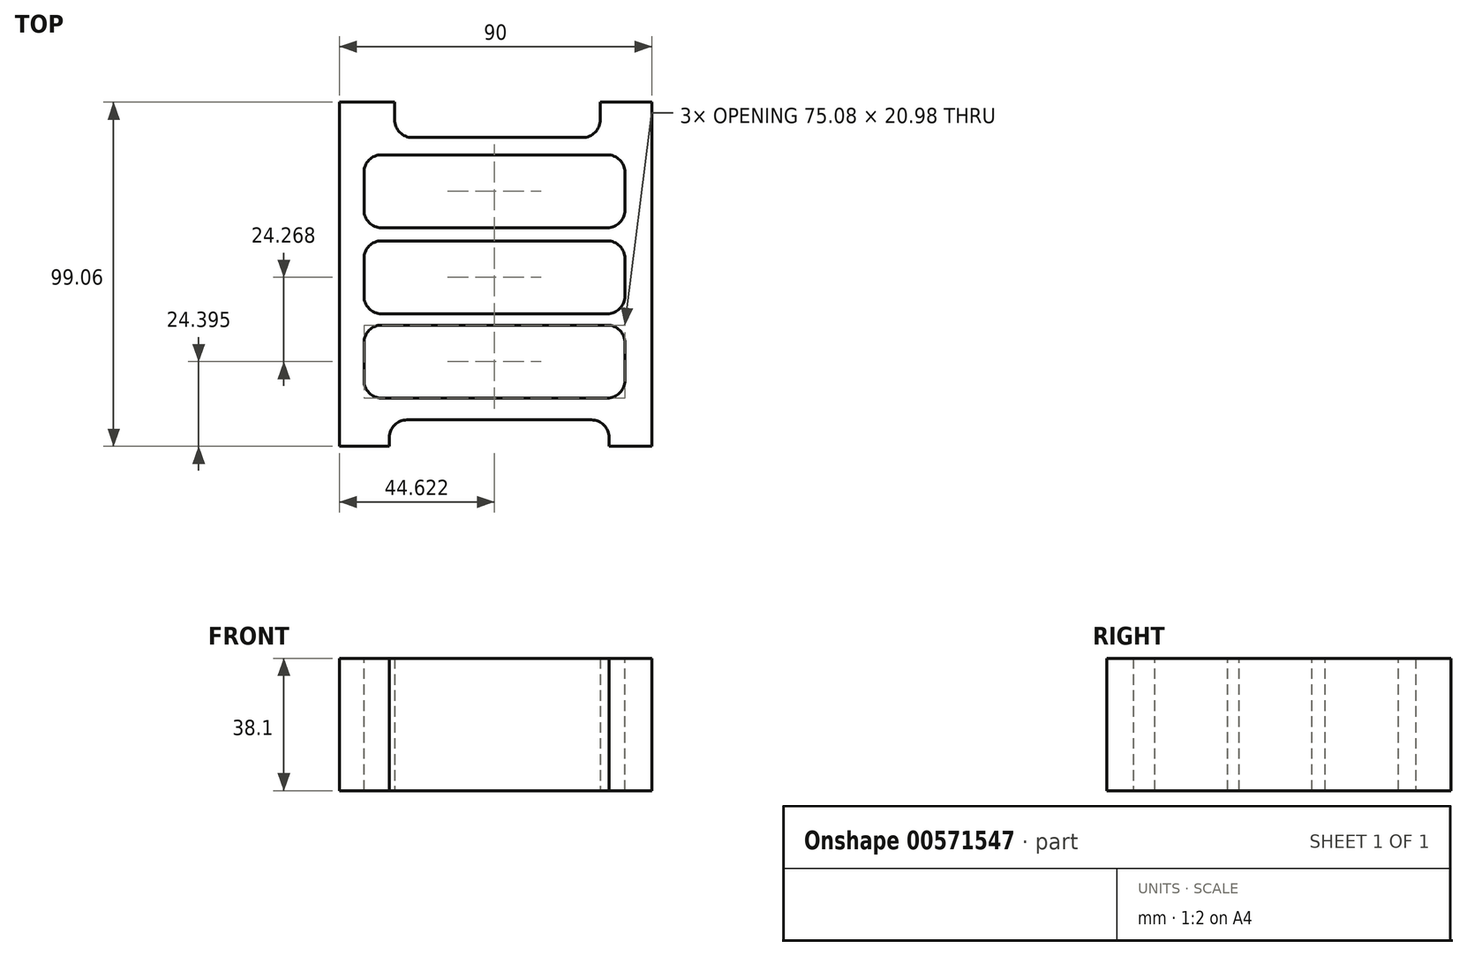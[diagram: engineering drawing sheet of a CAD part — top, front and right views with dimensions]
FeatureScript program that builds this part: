
annotation { "Feature Type Name" : "Feature", "Feature Type Description" : "" }
export const myFeature = defineFeature(function(context is Context, id is Id, definition is map)
    precondition{}
    {
        {
            var Q0;
            Q0=qCreatedBy(makeId("Top.planeOp"),FACE);
            var sketch = newSketch(context, id + "F0", { "sketchPlane" : qUnion([Q0])});
            skLineSegment(sketch, "E0.bottom", {"start": v(-48.92, 48.88) * mm, "end": v(41.08, 48.88) * mm});
            skLineSegment(sketch, "E0.top", {"start": v(-48.92, -50.18) * mm, "end": v(41.08, -50.18) * mm});
            skLineSegment(sketch, "E0.left", {"start": v(-48.92, 48.88) * mm, "end": v(-48.92, -50.18) * mm});
            skLineSegment(sketch, "E0.right", {"start": v(41.08, 48.88) * mm, "end": v(41.08, -50.18) * mm});
            skSolve(sketch);
        }
        {
            var Q0;
            Q0=makeQuery(id+"F0.imprint","IMPRINT",FACE,{"disambiguationData":[TD([[makeQuery(id+"F0.imprint","IMPRINT",EDGE,{"derivedFrom":sQuery(id+"F0.wireOp",EDGE,"E0.bottom")}),-1.0]])]});
            extrude(context, id + "F1", {"entities" : qUnion([Q0]), "depth" : 38.1 * mm, "offsetDistance" : 25.4 * mm});
        }
        {
            var Q0;
            Q0=makeQuery(id+"F1.opExtrude","CAP_FACE",FACE,{"disambiguationData":[OSD([sQuery(id+"F0.wireOp",EDGE,"E0.bottom"),sQuery(id+"F0.wireOp",EDGE,"E0.top"),sQuery(id+"F0.wireOp",EDGE,"E0.left"),sQuery(id+"F0.wireOp",EDGE,"E0.right")])],"isStart":false});
            var sketch = newSketch(context, id + "F2", { "sketchPlane" : qUnion([Q0])});
            skLineSegment(sketch, "E1.bottom", {"start": v(-41.84, 33.75) * mm, "end": v(33.24, 33.75) * mm});
            skLineSegment(sketch, "E1.top", {"start": v(-41.84, 12.77) * mm, "end": v(33.24, 12.77) * mm});
            skLineSegment(sketch, "E1.left", {"start": v(-41.84, 33.75) * mm, "end": v(-41.84, 12.77) * mm});
            skLineSegment(sketch, "E1.right", {"start": v(33.24, 33.75) * mm, "end": v(33.24, 12.77) * mm});
            skLineSegment(sketch, "E2.bottom", {"start": v(-41.84, 8.97) * mm, "end": v(33.24, 8.97) * mm});
            skLineSegment(sketch, "E2.top", {"start": v(-41.84, -12) * mm, "end": v(33.24, -12) * mm});
            skLineSegment(sketch, "E2.left", {"start": v(-41.84, 8.97) * mm, "end": v(-41.84, -12) * mm});
            skLineSegment(sketch, "E2.right", {"start": v(33.24, 8.97) * mm, "end": v(33.24, -12) * mm});
            skLineSegment(sketch, "E3.bottom", {"start": v(-41.84, -15.3) * mm, "end": v(33.24, -15.3) * mm});
            skLineSegment(sketch, "E3.top", {"start": v(-41.84, -36.28) * mm, "end": v(33.24, -36.28) * mm});
            skLineSegment(sketch, "E3.left", {"start": v(-41.84, -15.3) * mm, "end": v(-41.84, -36.28) * mm});
            skLineSegment(sketch, "E3.right", {"start": v(33.24, -15.3) * mm, "end": v(33.24, -36.28) * mm});
            skSolve(sketch);
        }
        {
            var Q0;
            Q0=makeQuery(id+"F2.imprint","IMPRINT",FACE,{"disambiguationData":[TD([[makeQuery(id+"F2.imprint","IMPRINT",EDGE,{"derivedFrom":sQuery(id+"F2.wireOp",EDGE,"E1.bottom")}),-1.0]])]});
            var Q1;
            Q1=makeQuery(id+"F2.imprint","IMPRINT",FACE,{"disambiguationData":[TD([[makeQuery(id+"F2.imprint","IMPRINT",EDGE,{"derivedFrom":sQuery(id+"F2.wireOp",EDGE,"E2.bottom")}),-1.0]])]});
            var Q2;
            Q2=makeQuery(id+"F2.imprint","IMPRINT",FACE,{"disambiguationData":[TD([[makeQuery(id+"F2.imprint","IMPRINT",EDGE,{"derivedFrom":sQuery(id+"F2.wireOp",EDGE,"E3.bottom")}),-1.0]])]});
            extrude(context, id + "F3", {"entities" : qUnion([Q0, Q1, Q2]), "operationType" : NewBodyOperationType.REMOVE, "oppositeDirection" : true, "depth" : 38.1 * mm, "offsetDistance" : 25.4 * mm});
        }
        {
            var Q0;
            Q0=makeQuery(id+"F3.boolean.opBoolean","COPY",EDGE,{"derivedFrom":makeQuery(id+"F3.opExtrude","SWEPT_EDGE",EDGE,{"disambiguationData":[OSD([sQuery(id+"F2.wireOp",EDGE,"E1.bottom"),sQuery(id+"F2.wireOp",EDGE,"E1.right")])]})});
            var Q1;
            Q1=makeQuery(id+"F3.boolean.opBoolean","COPY",EDGE,{"derivedFrom":makeQuery(id+"F3.opExtrude","SWEPT_EDGE",EDGE,{"disambiguationData":[OSD([sQuery(id+"F2.wireOp",EDGE,"E2.bottom"),sQuery(id+"F2.wireOp",EDGE,"E2.right")])]})});
            var Q2;
            Q2=makeQuery(id+"F3.boolean.opBoolean","COPY",EDGE,{"derivedFrom":makeQuery(id+"F3.opExtrude","SWEPT_EDGE",EDGE,{"disambiguationData":[OSD([sQuery(id+"F2.wireOp",EDGE,"E3.bottom"),sQuery(id+"F2.wireOp",EDGE,"E3.right")])]})});
            var Q3;
            Q3=makeQuery(id+"F3.boolean.opBoolean","COPY",EDGE,{"derivedFrom":makeQuery(id+"F3.opExtrude","SWEPT_EDGE",EDGE,{"disambiguationData":[OSD([sQuery(id+"F2.wireOp",EDGE,"E1.bottom"),sQuery(id+"F2.wireOp",EDGE,"E1.left")])]})});
            var Q4;
            Q4=makeQuery(id+"F3.boolean.opBoolean","COPY",EDGE,{"derivedFrom":makeQuery(id+"F3.opExtrude","SWEPT_EDGE",EDGE,{"disambiguationData":[OSD([sQuery(id+"F2.wireOp",EDGE,"E2.bottom"),sQuery(id+"F2.wireOp",EDGE,"E2.left")])]})});
            var Q5;
            Q5=makeQuery(id+"F3.boolean.opBoolean","COPY",EDGE,{"derivedFrom":makeQuery(id+"F3.opExtrude","SWEPT_EDGE",EDGE,{"disambiguationData":[OSD([sQuery(id+"F2.wireOp",EDGE,"E3.bottom"),sQuery(id+"F2.wireOp",EDGE,"E3.left")])]})});
            var Q6;
            Q6=makeQuery(id+"F3.boolean.opBoolean","COPY",EDGE,{"derivedFrom":makeQuery(id+"F3.opExtrude","SWEPT_EDGE",EDGE,{"disambiguationData":[OSD([sQuery(id+"F2.wireOp",EDGE,"E3.top"),sQuery(id+"F2.wireOp",EDGE,"E3.left")])]})});
            var Q7;
            Q7=makeQuery(id+"F3.boolean.opBoolean","COPY",EDGE,{"derivedFrom":makeQuery(id+"F3.opExtrude","SWEPT_EDGE",EDGE,{"disambiguationData":[OSD([sQuery(id+"F2.wireOp",EDGE,"E2.top"),sQuery(id+"F2.wireOp",EDGE,"E2.left")])]})});
            var Q8;
            Q8=makeQuery(id+"F3.boolean.opBoolean","COPY",EDGE,{"derivedFrom":makeQuery(id+"F3.opExtrude","SWEPT_EDGE",EDGE,{"disambiguationData":[OSD([sQuery(id+"F2.wireOp",EDGE,"E1.top"),sQuery(id+"F2.wireOp",EDGE,"E1.left")])]})});
            var Q9;
            Q9=makeQuery(id+"F3.boolean.opBoolean","COPY",EDGE,{"derivedFrom":makeQuery(id+"F3.opExtrude","SWEPT_EDGE",EDGE,{"disambiguationData":[OSD([sQuery(id+"F2.wireOp",EDGE,"E3.top"),sQuery(id+"F2.wireOp",EDGE,"E3.right")])]})});
            var Q10;
            Q10=makeQuery(id+"F3.boolean.opBoolean","COPY",EDGE,{"derivedFrom":makeQuery(id+"F3.opExtrude","SWEPT_EDGE",EDGE,{"disambiguationData":[OSD([sQuery(id+"F2.wireOp",EDGE,"E2.top"),sQuery(id+"F2.wireOp",EDGE,"E2.right")])]})});
            var Q11;
            Q11=makeQuery(id+"F3.boolean.opBoolean","COPY",EDGE,{"derivedFrom":makeQuery(id+"F3.opExtrude","SWEPT_EDGE",EDGE,{"disambiguationData":[OSD([sQuery(id+"F2.wireOp",EDGE,"E1.top"),sQuery(id+"F2.wireOp",EDGE,"E1.right")])]})});
            fillet(context, id + "F4", {"entities" : qUnion([Q0, Q1, Q2, Q3, Q4, Q5, Q6, Q7, Q8, Q9, Q10, Q11]), "radius" : 5.08 * mm, "tangentPropagation" : true, "allowEdgeOverflow" : false});
        }
        {
            var Q0;
            Q0=makeQuery(id+"F1.opExtrude","SWEPT_FACE",FACE,{"disambiguationData":[OSD([sQuery(id+"F0.wireOp",EDGE,"E0.bottom")])]});
            var sketch = newSketch(context, id + "F5", { "sketchPlane" : qUnion([Q0])});
            skLineSegment(sketch, "E4.bottom", {"start": v(-26.16, 38.1) * mm, "end": v(32.99, 38.1) * mm});
            skLineSegment(sketch, "E4.top", {"start": v(-26.16, 0) * mm, "end": v(32.99, 0) * mm});
            skLineSegment(sketch, "E4.left", {"start": v(-26.16, 38.1) * mm, "end": v(-26.16, 0) * mm});
            skLineSegment(sketch, "E4.right", {"start": v(32.99, 38.1) * mm, "end": v(32.99, 0) * mm});
            skSolve(sketch);
        }
        {
            var Q0;
            Q0=makeQuery(id+"F5.imprint","IMPRINT",FACE,{"disambiguationData":[TD([[makeQuery(id+"F5.imprint","IMPRINT",EDGE,{"derivedFrom":sQuery(id+"F5.wireOp",EDGE,"E4.bottom")}),1.0]])]});
            extrude(context, id + "F6", {"entities" : qUnion([Q0]), "operationType" : NewBodyOperationType.REMOVE, "oppositeDirection" : true, "depth" : 10.16 * mm, "offsetDistance" : 25.4 * mm});
        }
        {
            var Q0;
            Q0=makeQuery(id+"F6.boolean.opBoolean","COPY",EDGE,{"derivedFrom":makeQuery(id+"F6.opExtrude","CAP_EDGE",EDGE,{"disambiguationData":[OSD([sQuery(id+"F5.wireOp",EDGE,"E4.right")])],"isStart":false})});
            var Q1;
            Q1=makeQuery(id+"F6.boolean.opBoolean","COPY",EDGE,{"derivedFrom":makeQuery(id+"F6.opExtrude","CAP_EDGE",EDGE,{"disambiguationData":[OSD([sQuery(id+"F5.wireOp",EDGE,"E4.left")])],"isStart":false})});
            fillet(context, id + "F7", {"entities" : qUnion([Q0, Q1]), "radius" : 5.08 * mm, "tangentPropagation" : true, "allowEdgeOverflow" : false});
        }
        {
            var Q0;
            Q0=makeQuery(id+"F1.opExtrude","SWEPT_FACE",FACE,{"disambiguationData":[OSD([sQuery(id+"F0.wireOp",EDGE,"E0.top")])]});
            var sketch = newSketch(context, id + "F8", { "sketchPlane" : qUnion([Q0])});
            skLineSegment(sketch, "E5.bottom", {"start": v(-34.5, 38.1) * mm, "end": v(28.7, 38.1) * mm});
            skLineSegment(sketch, "E5.top", {"start": v(-34.5, 0) * mm, "end": v(28.7, 0) * mm});
            skLineSegment(sketch, "E5.left", {"start": v(-34.5, 38.1) * mm, "end": v(-34.5, 0) * mm});
            skLineSegment(sketch, "E5.right", {"start": v(28.7, 38.1) * mm, "end": v(28.7, 0) * mm});
            skSolve(sketch);
        }
        {
            var Q0;
            Q0=makeQuery(id+"F8.imprint","IMPRINT",FACE,{"disambiguationData":[TD([[makeQuery(id+"F8.imprint","IMPRINT",EDGE,{"derivedFrom":sQuery(id+"F8.wireOp",EDGE,"E5.bottom")}),-1.0]])]});
            extrude(context, id + "F9", {"entities" : qUnion([Q0]), "operationType" : NewBodyOperationType.REMOVE, "oppositeDirection" : true, "depth" : 7.62 * mm, "offsetDistance" : 25.4 * mm});
        }
        {
            var Q0;
            Q0=makeQuery(id+"F9.boolean.opBoolean","COPY",EDGE,{"derivedFrom":makeQuery(id+"F9.opExtrude","CAP_EDGE",EDGE,{"disambiguationData":[OSD([sQuery(id+"F8.wireOp",EDGE,"E5.right")])],"isStart":false})});
            var Q1;
            Q1=makeQuery(id+"F9.boolean.opBoolean","COPY",EDGE,{"derivedFrom":makeQuery(id+"F9.opExtrude","CAP_EDGE",EDGE,{"disambiguationData":[OSD([sQuery(id+"F8.wireOp",EDGE,"E5.left")])],"isStart":false})});
            fillet(context, id + "F10", {"entities" : qUnion([Q0, Q1]), "radius" : 5.08 * mm, "tangentPropagation" : true, "allowEdgeOverflow" : false});
        }
    });
